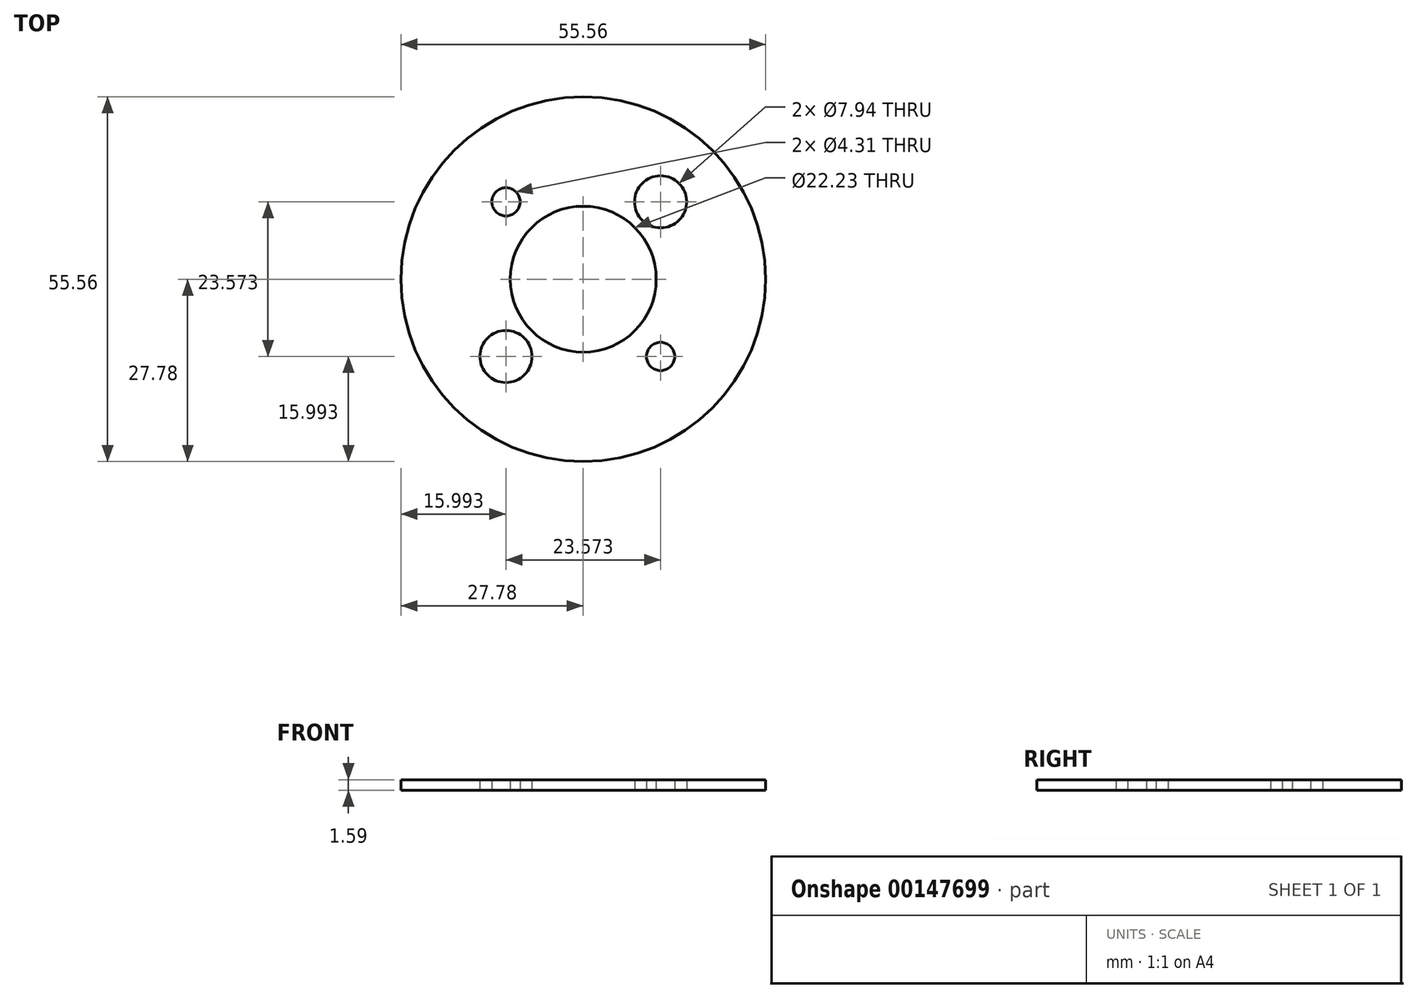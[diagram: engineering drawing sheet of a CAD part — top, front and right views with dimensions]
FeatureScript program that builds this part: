
annotation { "Feature Type Name" : "Feature", "Feature Type Description" : "" }
export const myFeature = defineFeature(function(context is Context, id is Id, definition is map)
    precondition{}
    {
        {
            var Q0;
            Q0=qCreatedBy(makeId("Top.planeOp"),FACE);
            var sketch = newSketch(context, id + "F0", { "sketchPlane" : qUnion([Q0])});
            skCircle(sketch, "E0", {"center": v(0, 0) * mm, "radius": 27.78 * mm});
            skLineSegment(sketch, "E1.bottom", {"start": v(-11.79, 11.79) * mm, "end": v(11.79, 11.79) * mm, "construction": true});
            skLineSegment(sketch, "E1.top", {"start": v(-11.79, -11.79) * mm, "end": v(11.79, -11.79) * mm, "construction": true});
            skLineSegment(sketch, "E1.left", {"start": v(-11.79, 11.79) * mm, "end": v(-11.79, -11.79) * mm, "construction": true});
            skLineSegment(sketch, "E1.right", {"start": v(11.79, 11.79) * mm, "end": v(11.79, -11.79) * mm, "construction": true});
            skCircle(sketch, "E2", {"center": v(-11.79, 11.79) * mm, "radius": 5.56 * mm, "construction": true});
            skCircle(sketch, "E3", {"center": v(11.79, 11.79) * mm, "radius": 3.97 * mm});
            skCircle(sketch, "E4", {"center": v(-11.79, 11.79) * mm, "radius": 2.15 * mm});
            skCircle(sketch, "E5", {"center": v(-11.79, -11.79) * mm, "radius": 3.97 * mm});
            skCircle(sketch, "E6", {"center": v(11.79, -11.79) * mm, "radius": 2.15 * mm});
            skCircle(sketch, "E7", {"center": v(0, 0) * mm, "radius": 11.11 * mm});
            skSolve(sketch);
        }
        {
            var Q0;
            Q0=qSketchRegion(id+"F0",true);
            extrude(context, id + "F1", {"entities" : qUnion([Q0]), "depth" : 1.59 * mm});
        }
    });
